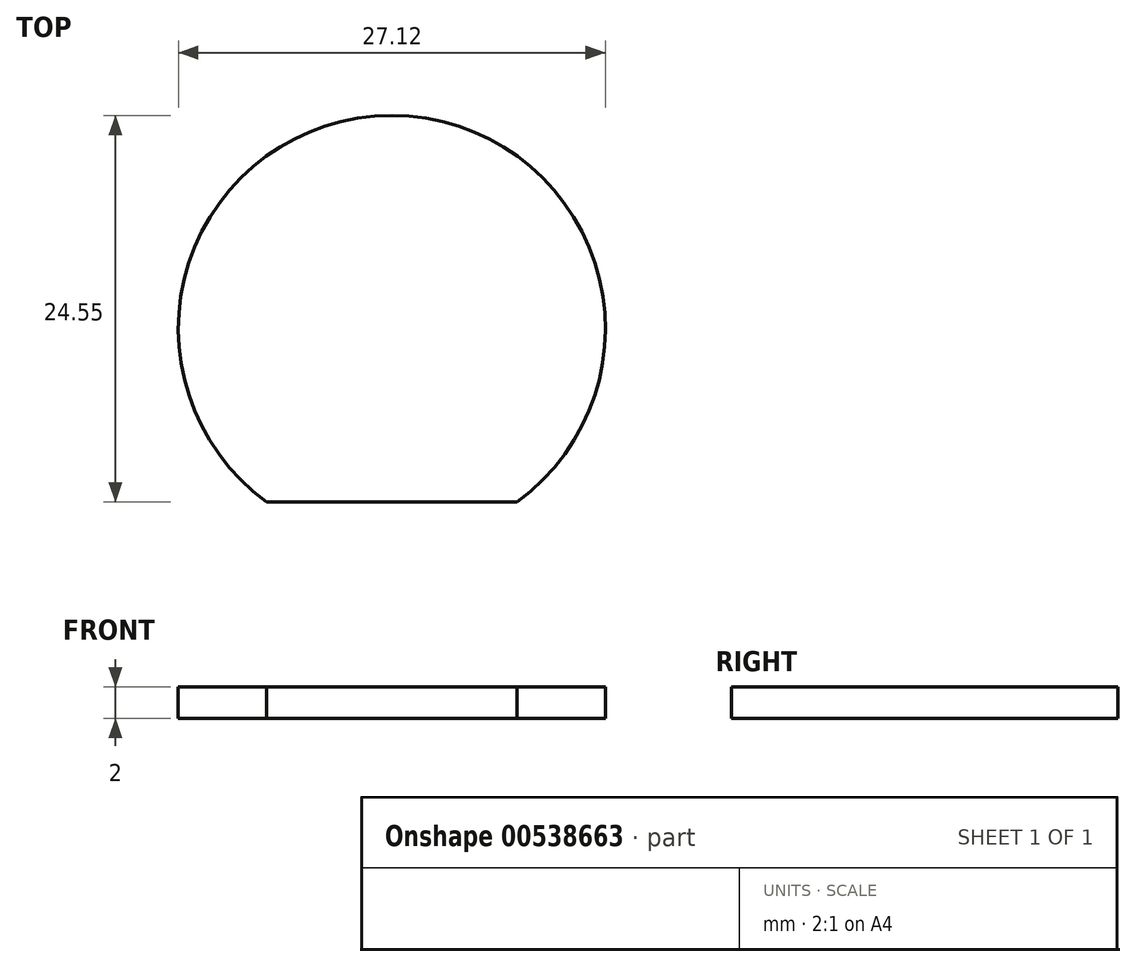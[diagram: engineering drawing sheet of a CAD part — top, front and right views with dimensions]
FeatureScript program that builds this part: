
annotation { "Feature Type Name" : "Feature", "Feature Type Description" : "" }
export const myFeature = defineFeature(function(context is Context, id is Id, definition is map)
    precondition{}
    {
        {
            var Q0;
            Q0=qCreatedBy(makeId("Top.planeOp"),FACE);
            var sketch = newSketch(context, id + "F0", { "sketchPlane" : qUnion([Q0])});
            skArc(sketch, "E0", {"start": v(7.95, -10.99) * mm, "mid": v(0, 13.56) * mm, "end": v(-7.95, -10.99) * mm});
            skLineSegment(sketch, "E1", {"start": v(-7.95, -10.99) * mm, "end": v(7.95, -10.99) * mm});
            skSolve(sketch);
        }
        {
            var Q0;
            Q0=makeQuery(id+"F0.imprint","IMPRINT",FACE,{"disambiguationData":[TD([[makeQuery(id+"F0.imprint","IMPRINT",EDGE,{"derivedFrom":sQuery(id+"F0.wireOp",EDGE,"E0")}),1.0]])]});
            extrude(context, id + "F1", {"entities" : qUnion([Q0]), "depth" : 2 * mm, "offsetDistance" : 25 * mm});
        }
    });
